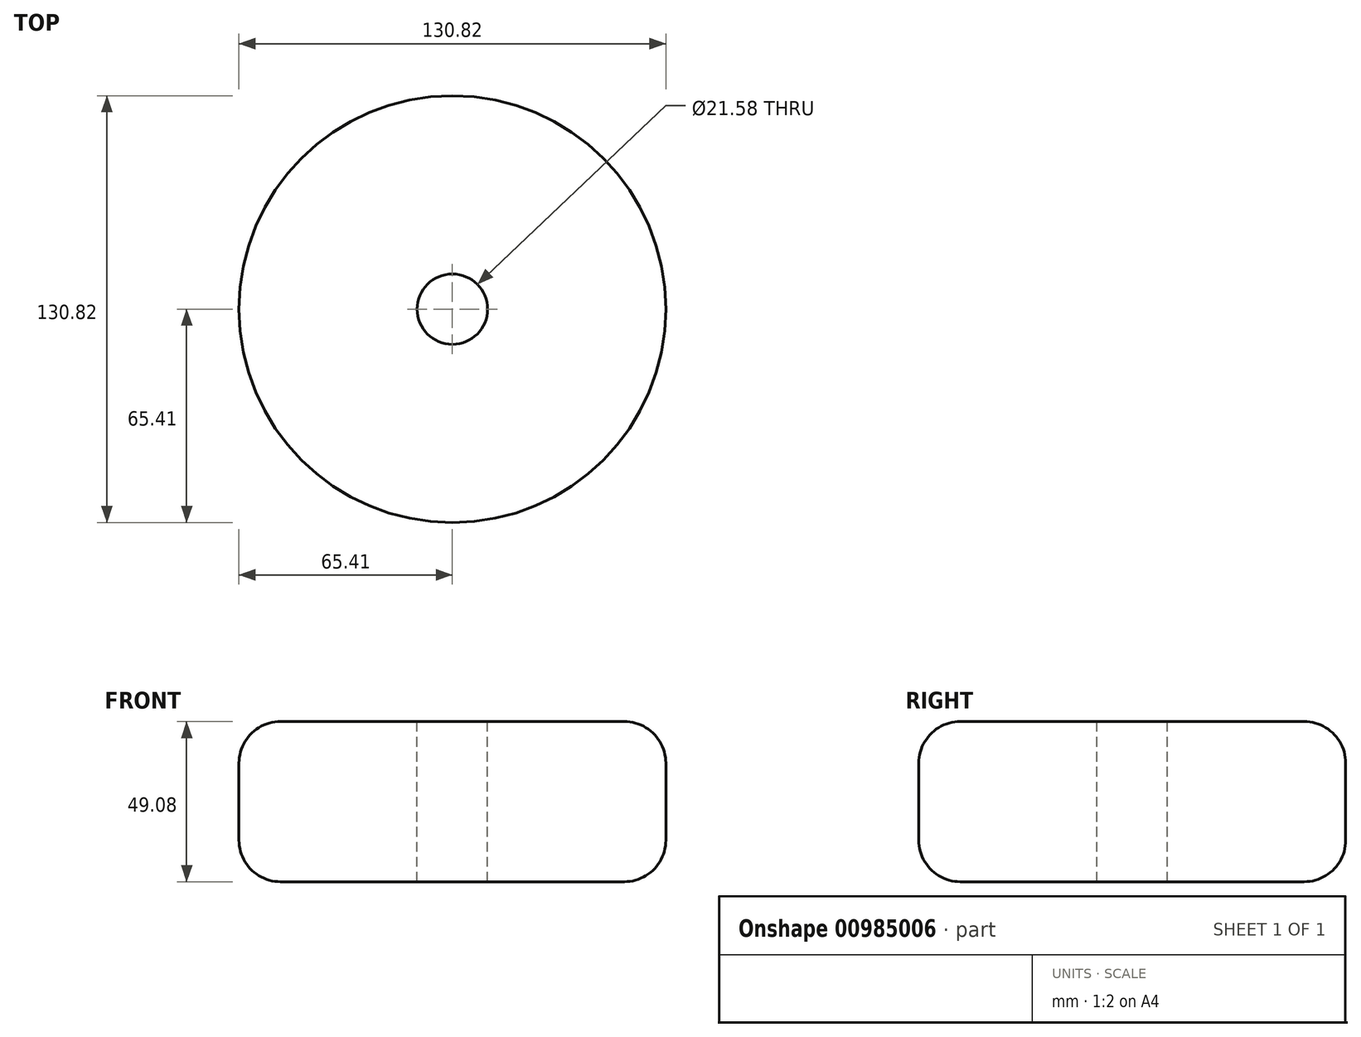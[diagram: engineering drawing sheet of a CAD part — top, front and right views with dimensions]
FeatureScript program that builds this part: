
annotation { "Feature Type Name" : "Feature", "Feature Type Description" : "" }
export const myFeature = defineFeature(function(context is Context, id is Id, definition is map)
    precondition{}
    {
        {
            var Q0;
            Q0=qCreatedBy(makeId("Front.planeOp"),FACE);
            var sketch = newSketch(context, id + "F0", { "sketchPlane" : qUnion([Q0])});
            skLineSegment(sketch, "E0", {"start": v(0, 12.7) * mm, "end": v(0, -12.7) * mm, "construction": true});
            skCircle(sketch, "E1", {"center": v(38.1, 0) * mm, "radius": 12.7 * mm});
            skLineSegment(sketch, "E2.bottom", {"start": v(10.79, 24.54) * mm, "end": v(65.41, 24.54) * mm});
            skLineSegment(sketch, "E2.top", {"start": v(10.79, -24.54) * mm, "end": v(65.41, -24.54) * mm});
            skLineSegment(sketch, "E2.left", {"start": v(10.79, 24.54) * mm, "end": v(10.79, -24.54) * mm});
            skLineSegment(sketch, "E2.right", {"start": v(65.41, 24.54) * mm, "end": v(65.41, -24.54) * mm});
            skSolve(sketch);
        }
        {
            var Q0;
            Q0=makeQuery(id+"F0.imprint","IMPRINT",FACE,{"disambiguationData":[TD([[makeQuery(id+"F0.imprint","IMPRINT",EDGE,{"derivedFrom":sQuery(id+"F0.wireOp",EDGE,"E1")}),-1.0]])]});
            var Q1;
            Q1=makeQuery(id+"F0.imprint","IMPRINT",FACE,{"disambiguationData":[TD([[makeQuery(id+"F0.imprint","IMPRINT",EDGE,{"derivedFrom":sQuery(id+"F0.wireOp",EDGE,"E1")}),1.0]])]});
            var Q2;
            Q2=sQuery(id+"F0.wireOp",EDGE,"E0");
            revolve(context, id + "F1", {"surfaceOperationType" : NewSurfaceOperationType.NEW, "entities" : qUnion([Q0, Q1]), "axis" : qUnion([Q2]), "revolveType" : RevolveType.FULL});
        }
        {
            var Q0;
            Q0=makeQuery(id+"F1.opRevolve","SWEPT_EDGE",EDGE,{"disambiguationData":[OSD([sQuery(id+"F0.wireOp",EDGE,"E2.bottom"),sQuery(id+"F0.wireOp",EDGE,"E2.right")])]});
            var Q1;
            Q1=makeQuery(id+"F1.opRevolve","SWEPT_EDGE",EDGE,{"disambiguationData":[OSD([sQuery(id+"F0.wireOp",EDGE,"E2.top"),sQuery(id+"F0.wireOp",EDGE,"E2.right")])]});
            fillet(context, id + "F2", {"entities" : qUnion([Q0, Q1]), "radius" : 12.7 * mm, "tangentPropagation" : true, "allowEdgeOverflow" : false});
        }
    });
